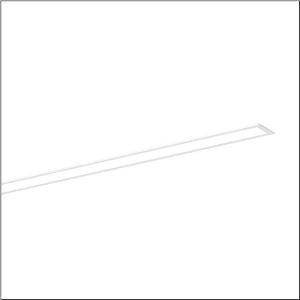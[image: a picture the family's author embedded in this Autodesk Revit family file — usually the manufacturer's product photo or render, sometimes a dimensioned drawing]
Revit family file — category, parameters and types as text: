
# Revit family: silica_r__21_51mx10da32wb_2fdc
name_source: partatom
category: Lighting Fixtures
units: mm (PartAtom-declared; Revit-internal decimal feet)

## family parameters
Cut with Voids When Loaded = No
Host = Face
Light Source = No
Part Type = Normal
Room Calculation Point = No
Round Connector Dimension = Use Diameter
Shared = No

## types (1)
- --- (1 x LED, 2400 lm, 16.1 W, 3000K)
    Apparent Load = 16 VA
    CIE Flux Codes = 48 79 96 100 100
    Color Rendering = 80
    Color Temperature = 3000K
    Default Elevation = 1800 mm
    Description = Silica® 21, office luminaire, primary optical cover: cover, of PMMA, opal, light emission: direct distribution, primary light characteristic: symmetric, installation type: recessed, LED, rated luminous flux: 2.400lm, luminous efficacy: 149lm/W, light colour: 830, colour temperature: 3000K, with terminal, 3+2-pole, max. 2.5mm², mains connection: 220..240V, AC, 50/60Hz, rated input power: 16.1W, luminaire housing, of aluminium, traffic white (RAL 9016), length: 1.228mm, width: 79mm, height: 53mm, protection rating (complete): IP20, insulation class (complete): insulation class I (protective earthing), certification: CE, permissible operating ambient temperature: 0..+35°C, standard: EN 50419, packaging unit: 1 piece
    Height = 0 mm  [stored 0 ft]
    Lamp = 1 x LED
    Lamp Light Flux = 2400 lm
    Lamp Power = 16.1 W
    Lamp count = 1
    Length = 1227 mm
    Luminous efficacy = 149 lm/W
    Manufacturer = Siteco
    ModVariant = No
    Model = 51MX10DA32WB
    Mounting Place = Ceiling
    Mounting Type = Recessed
    Number of Poles = 1
    OnlyDefault = Yes
    Power Factor = 1
    Product Name = Silica® 21
    Product group = office luminaire | ceiling recessed
    ProductGroupID = 401
    Protection Class = Protection class I
    Protection Degree = IP 20
    RLX_Detail_Level = 1
    RLX_Emergency_Light_Flux = 0 lm
    RLX_Emergency_Type = 0
    RLX_Emergency_Type_DB = No
    RlxData = <blob elided: 20989 chars, md5=866b14c8>
    Socket = socket
    Standby Power = 0 W
    System Light Flux = 2400 lm
    System Power = 16 W
    Type Comments = factory setting: luminous flux: 100 % | dim-lin: 254 | 233 mA
    Type Image = l_1297737.jpg
    URL = http://relux.com
    VarID = @adj_047757
    Voltage = 0 V
    Weight = 0.00 kg
    Width = 79 mm

note: [stored X ft] marks values corroborated as IEEE doubles in the binary element streams (Revit-internal decimal feet)

## geometry (parser evidence)
native form markers: Blend x4, Sweep x11
no freeform markers — native parametric forms only
